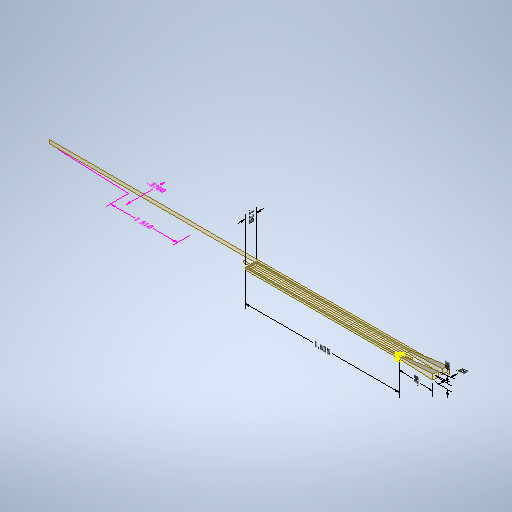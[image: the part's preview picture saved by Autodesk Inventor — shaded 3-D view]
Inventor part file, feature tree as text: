
AUTODESK INVENTOR PART (.ipt)
format: ipt  version: 2025.2 (Build 292293000, 293)  size: 322,560 bytes
history: native  units: in
note: dims shown in document units (in); Inventor stores cm internally (conversion verified against a paired STEP export)
features: other x9, plane x4, sketch x4, sweep x1, loft x1, mirror x1, projected_geometry x1
ambient origin geometry x8: Origin, YZ Plane, XZ Plane, XY Plane, X Axis, Y Axis, Z Axis, Center Point
bodies: Solid1 (feature_tree)
feature tree (21):
  other  "Annotations"
  sweep  "Sweep1"
  plane  "Work Plane1"
  plane  "Work Plane2"
  plane  "Work Plane4"
  sketch  "Sketch15"  dims[d86=-0.1175in]
  sketch  "Sketch16"  dims[d89=0.1in d90=0.0in d91=0.0in d92=0.0in d98=0.02in d99=0.02in d100=0.055in d102=0.055in d104=0.0in d109=0.0in d110=90.0deg d111=0.0in d112=90.0deg d116=-0.06in d113=0.0in d114=0.3937in d115=0.12in d117=0.0in d118=0.1551in d119=0.3754in d120=0.0in d121=0.3937in d122=0.055in d123=0.0in d124=0.3937in d125=0.055in d126=1.635in d42=0.2341in d43=0.169in d44=0.37in d48=0.2141in d49=0.2512in d50=1.51in]
  loft  "Loft3"
  plane  "Work Plane5"
  mirror  "Mirror3"
  sketch  "Sketch1"  dims[d6=0.0in d7=0.0in d11=0.375in d19=-0.25in]
  sketch  "Sketch2"  dims[d69=1.625in d70=1.625in]
  projected_geometry  "Projected Loop1"
  other  "Edges4"
  other  "Linear Dimension 1"
  other  "Linear Dimension 3"
  other  "Linear Dimension 4"
  other  "Linear Dimension 5"
  other  "Linear Dimension 6"
  other  "Linear Dimension 7"
  other  "Linear Dimension 8"
